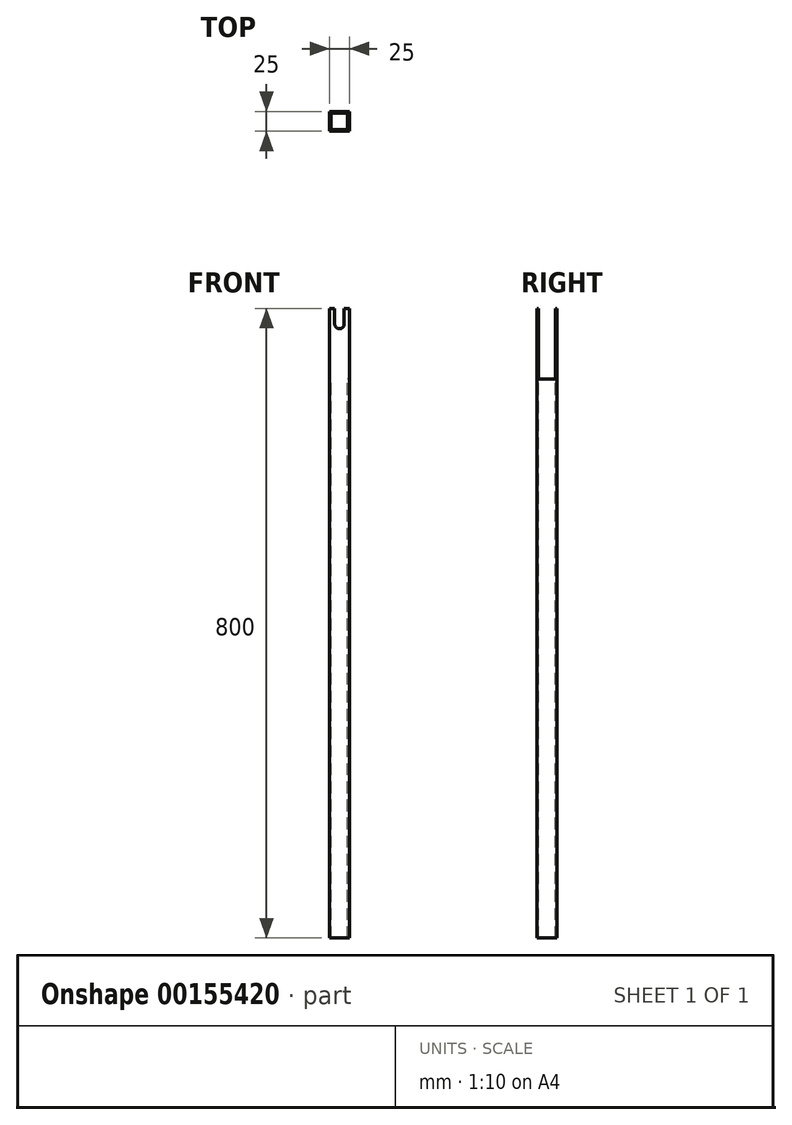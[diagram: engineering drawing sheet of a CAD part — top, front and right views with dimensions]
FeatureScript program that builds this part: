
annotation { "Feature Type Name" : "Feature", "Feature Type Description" : "" }
export const myFeature = defineFeature(function(context is Context, id is Id, definition is map)
    precondition{}
    {
        {
            var Q0;
            Q0=qCreatedBy(makeId("Top.planeOp"),FACE);
            var sketch = newSketch(context, id + "F0", { "sketchPlane" : qUnion([Q0])});
            skLineSegment(sketch, "E0.bottom", {"start": v(12.5, 12.5) * mm, "end": v(-12.5, 12.5) * mm});
            skLineSegment(sketch, "E0.top", {"start": v(12.5, -12.5) * mm, "end": v(-12.5, -12.5) * mm});
            skLineSegment(sketch, "E0.left", {"start": v(12.5, 12.5) * mm, "end": v(12.5, -12.5) * mm});
            skLineSegment(sketch, "E0.right", {"start": v(-12.5, 12.5) * mm, "end": v(-12.5, -12.5) * mm});
            skPoint(sketch, "E0.middle", {"position": v(0, 0) * mm});
            skSolve(sketch);
        }
        {
            var Q0;
            Q0=makeQuery(id+"F0.imprint","IMPRINT",FACE,{"disambiguationData":[TD([[makeQuery(id+"F0.imprint","IMPRINT",EDGE,{"derivedFrom":sQuery(id+"F0.wireOp",EDGE,"E0.bottom")}),1.0]])]});
            extrude(context, id + "F1", {"entities" : qUnion([Q0]), "endBound" : BoundingType.SYMMETRIC, "depth" : 800 * mm});
        }
        {
            var Q0;
            Q0=makeQuery(id+"F1.opExtrude","CAP_FACE",FACE,{"disambiguationData":[OSD([sQuery(id+"F0.wireOp",EDGE,"E0.bottom"),sQuery(id+"F0.wireOp",EDGE,"E0.top"),sQuery(id+"F0.wireOp",EDGE,"E0.left"),sQuery(id+"F0.wireOp",EDGE,"E0.right")])],"isStart":false});
            var sketch = newSketch(context, id + "F2", { "sketchPlane" : qUnion([Q0])});
            skLineSegment(sketch, "E1.0", {"start": v(-10.5, 10.5) * mm, "end": v(-10.5, -10.5) * mm});
            skLineSegment(sketch, "E1.1", {"start": v(10.5, 10.5) * mm, "end": v(-10.5, 10.5) * mm});
            skLineSegment(sketch, "E1.2", {"start": v(10.5, 10.5) * mm, "end": v(10.5, -10.5) * mm});
            skLineSegment(sketch, "E1.3", {"start": v(10.5, -10.5) * mm, "end": v(-10.5, -10.5) * mm});
            skSolve(sketch);
        }
        {
            var Q0;
            Q0=makeQuery(id+"F2.imprint","IMPRINT",FACE,{"disambiguationData":[TD([[makeQuery(id+"F2.imprint","IMPRINT",EDGE,{"derivedFrom":sQuery(id+"F2.wireOp",EDGE,"E1.0")}),1.0]])]});
            extrude(context, id + "F3", {"entities" : qUnion([Q0]), "operationType" : NewBodyOperationType.REMOVE, "endBound" : BoundingType.THROUGH_ALL, "oppositeDirection" : true, "depth" : 25 * mm});
        }
        {
            var Q0;
            Q0=makeQuery(id+"F1.opExtrude","SWEPT_FACE",FACE,{"disambiguationData":[OSD([sQuery(id+"F0.wireOp",EDGE,"E0.right")])]});
            var sketch = newSketch(context, id + "F4", { "sketchPlane" : qUnion([Q0])});
            skLineSegment(sketch, "E2.bottom", {"start": v(10.5, 400) * mm, "end": v(-10.5, 400) * mm});
            skLineSegment(sketch, "E2.top", {"start": v(10.5, 310) * mm, "end": v(-10.5, 310) * mm});
            skLineSegment(sketch, "E2.left", {"start": v(10.5, 400) * mm, "end": v(10.5, 310) * mm});
            skLineSegment(sketch, "E2.right", {"start": v(-10.5, 400) * mm, "end": v(-10.5, 310) * mm});
            skSolve(sketch);
        }
        {
            var Q0;
            Q0=makeQuery(id+"F4.imprint","IMPRINT",FACE,{"disambiguationData":[TD([[makeQuery(id+"F4.imprint","IMPRINT",EDGE,{"derivedFrom":sQuery(id+"F4.wireOp",EDGE,"E2.bottom")}),-1.0]])]});
            extrude(context, id + "F5", {"entities" : qUnion([Q0]), "operationType" : NewBodyOperationType.REMOVE, "endBound" : BoundingType.THROUGH_ALL, "oppositeDirection" : true, "depth" : 25 * mm});
        }
        {
            var Q0;
            Q0=makeQuery(id+"F1.opExtrude","SWEPT_FACE",FACE,{"disambiguationData":[OSD([sQuery(id+"F0.wireOp",EDGE,"E0.top")])]});
            var sketch = newSketch(context, id + "F6", { "sketchPlane" : qUnion([Q0])});
            skLineSegment(sketch, "E3.top", {"start": v(6, 400) * mm, "end": v(-6, 400) * mm});
            skLineSegment(sketch, "E3.left", {"start": v(6, 380) * mm, "end": v(6, 400) * mm});
            skLineSegment(sketch, "E3.right", {"start": v(-6, 380) * mm, "end": v(-6, 400) * mm});
            skArc(sketch, "E4", {"start": v(-6, 380) * mm, "mid": v(0, 374) * mm, "end": v(6, 380) * mm});
            skSolve(sketch);
        }
        {
            var Q0;
            Q0=makeQuery(id+"F6.imprint","IMPRINT",FACE,{"disambiguationData":[TD([[makeQuery(id+"F6.imprint","IMPRINT",EDGE,{"derivedFrom":sQuery(id+"F6.wireOp",EDGE,"E3.top")}),1.0]])]});
            extrude(context, id + "F7", {"entities" : qUnion([Q0]), "operationType" : NewBodyOperationType.REMOVE, "endBound" : BoundingType.THROUGH_ALL, "oppositeDirection" : true, "depth" : 25 * mm});
        }
    });
